# Revit family: Deca_Tubo de ligacao para bacia_Tubo Ligação_1968
name_source: partatom
category: Plumbing Fixtures
units: mm (PartAtom-declared; Revit-internal decimal feet)

## family parameters
Cut with Voids When Loaded = No
Host = Face
Part Type = Normal
Room Calculation Point = No
Round Connector Dimension = Use Radius
Shared = No

## types (7) — shared parameters
Acompanha o Produto = -
Aprovado por = quattroD
Atendimento ao Cliente = 0800-0117073
Categoria = COMPLEMENTARES
Composição Anel Vedação = -
Composição Assento = -
Composição Básica = Liga de Cobre (bronze e latão),Plásticos de Engenharia,Elastômeros
Composição Componente = -
Consumo = -
Cor Interna = -
Cor Secundária = -
Cores Componente = -
Criado por = quattroD
Código Pai = 1968
Default Elevation = 350 mm
Description = Tubo de ligação para bacia
Diâmetro Água Fria = 40 mm  [stored 0.131234 ft]
Informações Complementares = -
Itens de Instalação = -
Linha = Tubo Ligação
Manufacturer = Deca
Norma = Não Possui
Pressão máx. funcionamento = -
Pressão mín. Aquec. Acúmulo = -
Pressão mín. Aquec. Passagem = -
Pressão mín. funcionamento = -
Raio Água Fria = 20 mm
Saída de Esgoto = -
Segmento = Banheiro Competitivo
Tipo de dispositivo economizador = -
Tipo de mecanismo utilizado = -
Tipo de rosca de entrada = -
Tipo de rosca de saída = -
URL = www.deca.com.br
Vazão na Pressão máx. (L/min) = -
Vazão na Pressão mín. (L/min) = -
zero-valued in all types: CWFU

## per-type parameters (varying)
| type | Cor Principal | Material | Model | Peso Líquido (Kg) |
| 1968.C_Cromado | Cromado | Deca_Cromado | 1968.C | 0.18 |
| 1968.CT.MT_Corten | Corten | Deca_Corten | 1968.CT.MT | 0.255 |
| 1968.GL_Gold | Gold | Deca_Gold | 1968.GL | 0.255 |
| 1968.GL.MT_Gold Matte | Gold Matte | Deca_Gold Matte | 1968.GL.MT | 0.255 |
| 1968.GL.RD_Red Gold | Red Gold | Deca_Red Gold | 1968.GL.RD | 0.255 |
| 1968.BL.MT_Black Matte | Black Matte | Deca_Black Matte | 1968.BL.MT | 0.255 |
| 1968.BL.NO_Black Noir | Black Noir | Deca_Black Noir | 1968.BL.NO | 0.255 |

note: [stored X ft] marks values corroborated as IEEE doubles in the binary element streams (Revit-internal decimal feet)

## geometry (parser evidence)
native form markers: Sweep x2
no freeform markers — native parametric forms only
